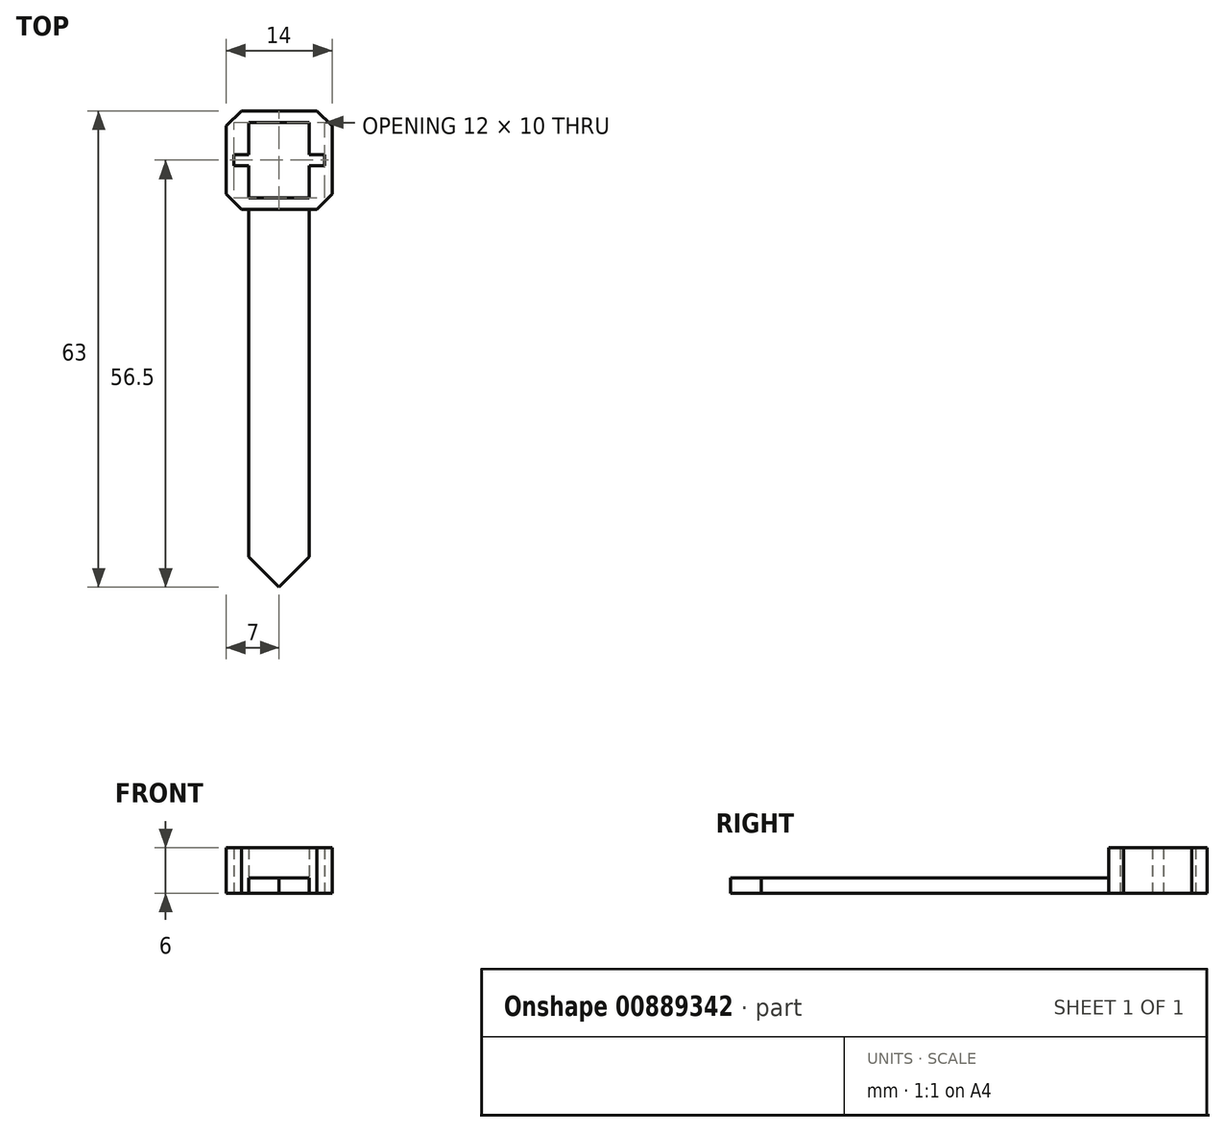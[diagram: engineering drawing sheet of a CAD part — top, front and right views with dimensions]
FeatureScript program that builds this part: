
annotation { "Feature Type Name" : "Feature", "Feature Type Description" : "" }
export const myFeature = defineFeature(function(context is Context, id is Id, definition is map)
    precondition{}
    {
        {
            var Q0;
            Q0=qCreatedBy(makeId("Top.planeOp"),FACE);
            var sketch = newSketch(context, id + "F0", { "sketchPlane" : qUnion([Q0])});
            skLineSegment(sketch, "E0.bottom", {"start": v(4, -5) * mm, "end": v(-4, -5) * mm});
            skLineSegment(sketch, "E0.top", {"start": v(4, 5) * mm, "end": v(-4, 5) * mm});
            skLineSegment(sketch, "E0.left", {"start": v(4, -5) * mm, "end": v(4, -0.75) * mm});
            skLineSegment(sketch, "E0.right", {"start": v(-4, -5) * mm, "end": v(-4, -0.75) * mm});
            skPoint(sketch, "E0.middle", {"position": v(0, 0) * mm});
            skLineSegment(sketch, "E1.bottom", {"start": v(7, -6.5) * mm, "end": v(-7, -6.5) * mm});
            skLineSegment(sketch, "E1.top", {"start": v(7, 6.5) * mm, "end": v(-7, 6.5) * mm});
            skLineSegment(sketch, "E1.left", {"start": v(7, -6.5) * mm, "end": v(7, 6.5) * mm});
            skLineSegment(sketch, "E1.right", {"start": v(-7, -6.5) * mm, "end": v(-7, 6.5) * mm});
            skLineSegment(sketch, "E2.bottom", {"start": v(6, -0.75) * mm, "end": v(4, -0.75) * mm});
            skLineSegment(sketch, "E2.top", {"start": v(6, 0.75) * mm, "end": v(4, 0.75) * mm});
            skLineSegment(sketch, "E2.left", {"start": v(6, -0.75) * mm, "end": v(6, 0.75) * mm});
            skLineSegment(sketch, "E2.right", {"start": v(-6, -0.75) * mm, "end": v(-6, 0.75) * mm});
            skLineSegment(sketch, "E3.trimOffspring", {"start": v(-4, -0.75) * mm, "end": v(-6, -0.75) * mm});
            skLineSegment(sketch, "E4.trimOffspring", {"start": v(-4, 0.75) * mm, "end": v(-4, 5) * mm});
            skLineSegment(sketch, "E5.trimOffspring", {"start": v(-4, 0.75) * mm, "end": v(-6, 0.75) * mm});
            skLineSegment(sketch, "E6.trimOffspring", {"start": v(4, 0.75) * mm, "end": v(4, 5) * mm});
            skLineSegment(sketch, "E7.bottom", {"start": v(4, -56.5) * mm, "end": v(-4, -56.5) * mm});
            skLineSegment(sketch, "E7.top", {"start": v(4, -6.5) * mm, "end": v(-4, -6.5) * mm});
            skLineSegment(sketch, "E7.left", {"start": v(4, -56.5) * mm, "end": v(4, -6.5) * mm});
            skLineSegment(sketch, "E7.right", {"start": v(-4, -56.5) * mm, "end": v(-4, -6.5) * mm});
            skPoint(sketch, "E7.middle", {"position": v(0, -31.5) * mm});
            skSolve(sketch);
        }
        {
            var Q0;
            Q0=makeQuery(id+"F0.imprint","IMPRINT",FACE,{"disambiguationData":[TD([[makeQuery(id+"F0.imprint","IMPRINT",EDGE,{"derivedFrom":sQuery(id+"F0.wireOp",EDGE,"E0.bottom")}),1.0]])]});
            extrude(context, id + "F1", {"entities" : qUnion([Q0]), "depth" : 6 * mm, "offsetDistance" : 25 * mm});
        }
        {
            var Q0;
            Q0=makeQuery(id+"F0.imprint","IMPRINT",FACE,{"disambiguationData":[TD([[makeQuery(id+"F0.imprint","IMPRINT",EDGE,{"derivedFrom":sQuery(id+"F0.wireOp",EDGE,"E7.bottom")}),-1.0]])]});
            extrude(context, id + "F2", {"entities" : qUnion([Q0]), "operationType" : NewBodyOperationType.ADD, "depth" : 2 * mm, "offsetDistance" : 25 * mm});
        }
        {
            var Q0;
            Q0=makeQuery(id+"F2.opExtrude","CAP_EDGE",EDGE,{"disambiguationData":[OSD([sQuery(id+"F0.wireOp",EDGE,"E1.bottom")])],"isStart":false});
            var Q1;
            Q1=makeQuery(id+"F2.opExtrude","SWEPT_EDGE",EDGE,{"disambiguationData":[OSD([sQuery(id+"F0.wireOp",EDGE,"E7.bottom"),sQuery(id+"F0.wireOp",EDGE,"E7.right")])]});
            var Q2;
            Q2=makeQuery(id+"F2.opExtrude","SWEPT_EDGE",EDGE,{"disambiguationData":[OSD([sQuery(id+"F0.wireOp",EDGE,"E7.bottom"),sQuery(id+"F0.wireOp",EDGE,"E7.left")])]});
            chamfer(context, id + "F3", {"entities" : qUnion([Q0, Q1, Q2]), "width" : 4 * mm, "tangentPropagation" : true});
        }
        {
            var Q0;
            Q0=makeQuery(id+"F1.opExtrude","SWEPT_EDGE",EDGE,{"disambiguationData":[OSD([sQuery(id+"F0.wireOp",EDGE,"E1.bottom"),sQuery(id+"F0.wireOp",EDGE,"E1.right")])]});
            var Q1;
            Q1=makeQuery(id+"F1.opExtrude","SWEPT_EDGE",EDGE,{"disambiguationData":[OSD([sQuery(id+"F0.wireOp",EDGE,"E1.top"),sQuery(id+"F0.wireOp",EDGE,"E1.right")])]});
            var Q2;
            Q2=makeQuery(id+"F1.opExtrude","SWEPT_EDGE",EDGE,{"disambiguationData":[OSD([sQuery(id+"F0.wireOp",EDGE,"E1.bottom"),sQuery(id+"F0.wireOp",EDGE,"E1.left")])]});
            var Q3;
            Q3=makeQuery(id+"F1.opExtrude","SWEPT_EDGE",EDGE,{"disambiguationData":[OSD([sQuery(id+"F0.wireOp",EDGE,"E1.top"),sQuery(id+"F0.wireOp",EDGE,"E1.left")])]});
            chamfer(context, id + "F4", {"entities" : qUnion([Q0, Q1, Q2, Q3]), "width" : 2 * mm, "tangentPropagation" : true});
        }
    });
